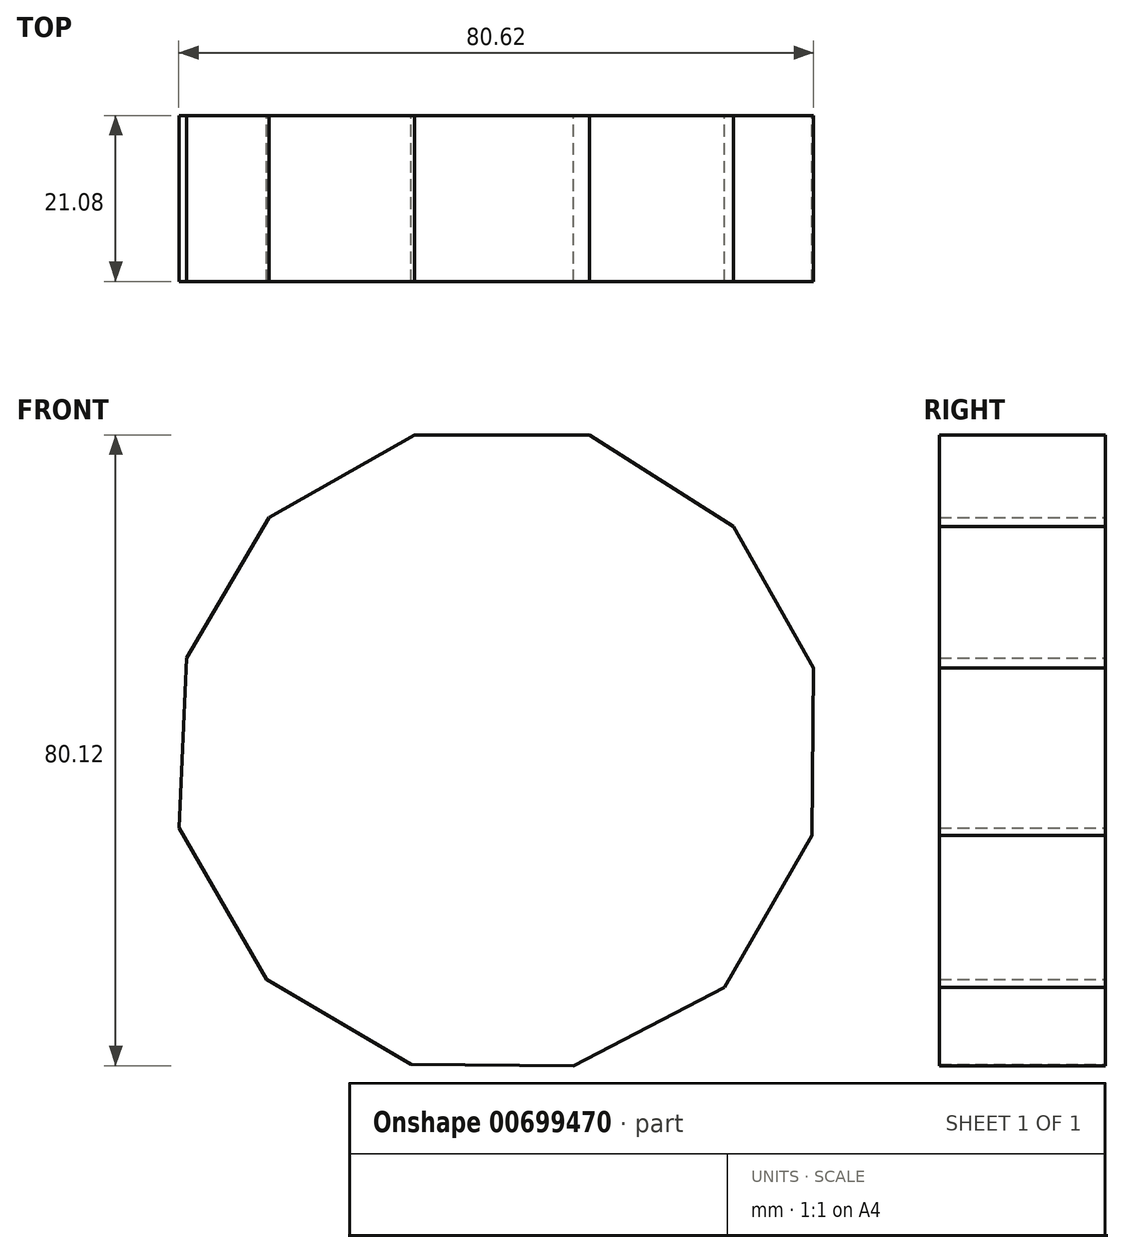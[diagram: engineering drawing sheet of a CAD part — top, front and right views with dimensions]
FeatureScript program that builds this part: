
annotation { "Feature Type Name" : "Feature", "Feature Type Description" : "" }
export const myFeature = defineFeature(function(context is Context, id is Id, definition is map)
    precondition{}
    {
        {
            var Q0;
            Q0=qCreatedBy(makeId("Front.planeOp"),FACE);
            var sketch = newSketch(context, id + "F0", { "sketchPlane" : qUnion([Q0])});
            skCircle(sketch, "E0.cCircle", {"center": v(0, 0) * mm, "radius": 76.52 * mm, "construction": true});
            skLineSegment(sketch, "E0.0", {"start": v(-76.41, 44.37) * mm, "end": v(0.21, 88.36) * mm});
            skLineSegment(sketch, "E0.1", {"start": v(0.21, 88.36) * mm, "end": v(76.63, 44) * mm});
            skLineSegment(sketch, "E0.2", {"start": v(76.63, 44) * mm, "end": v(76.41, -44.37) * mm});
            skLineSegment(sketch, "E0.3", {"start": v(76.41, -44.37) * mm, "end": v(-0.21, -88.36) * mm});
            skLineSegment(sketch, "E0.4", {"start": v(-0.21, -88.36) * mm, "end": v(-76.63, -44) * mm});
            skLineSegment(sketch, "E0.5", {"start": v(-76.63, -44) * mm, "end": v(-76.41, 44.37) * mm});
            skPoint(sketch, "E0.0.midPoint", {"position": v(-38.1, 66.36) * mm});
            skCircle(sketch, "E1.cCircle", {"center": v(0, 0) * mm, "radius": 40.02 * mm, "construction": true});
            skLineSegment(sketch, "E1.0", {"start": v(-80.05, 0.63) * mm, "end": v(40.57, 69) * mm});
            skLineSegment(sketch, "E1.1", {"start": v(40.57, 69) * mm, "end": v(39.48, -69.64) * mm});
            skLineSegment(sketch, "E1.2", {"start": v(39.48, -69.64) * mm, "end": v(-80.05, 0.63) * mm});
            skPoint(sketch, "E1.0.midPoint", {"position": v(-19.74, 34.82) * mm});
            skLineSegment(sketch, "E2.0", {"start": v(-36.9, 71.04) * mm, "end": v(79.97, -3.57) * mm});
            skLineSegment(sketch, "E2.1", {"start": v(79.97, -3.57) * mm, "end": v(-43.07, -67.47) * mm});
            skLineSegment(sketch, "E2.2", {"start": v(-43.07, -67.47) * mm, "end": v(-36.9, 71.04) * mm});
            skPoint(sketch, "E2.0.midPoint", {"position": v(21.54, 33.74) * mm});
            skLineSegment(sketch, "E3.0", {"start": v(-69.64, -39.48) * mm, "end": v(0.63, 80.05) * mm});
            skLineSegment(sketch, "E3.1", {"start": v(0.63, 80.05) * mm, "end": v(69, -40.57) * mm});
            skLineSegment(sketch, "E3.2", {"start": v(69, -40.57) * mm, "end": v(-69.64, -39.48) * mm});
            skPoint(sketch, "E3.0.midPoint", {"position": v(-34.5, 20.28) * mm});
            skLineSegment(sketch, "E4.0", {"start": v(-69.32, 40.02) * mm, "end": v(69.32, 40.02) * mm});
            skLineSegment(sketch, "E4.1", {"start": v(69.32, 40.02) * mm, "end": v(0, -80.05) * mm});
            skLineSegment(sketch, "E4.2", {"start": v(0, -80.05) * mm, "end": v(-69.32, 40.02) * mm});
            skPoint(sketch, "E4.0.midPoint", {"position": v(0, 40.02) * mm});
            skCircle(sketch, "E5.cCircle", {"center": v(0, 0) * mm, "radius": 17.05 * mm, "construction": true});
            skLineSegment(sketch, "E5.0", {"start": v(-34.1, 0.2) * mm, "end": v(17.21, 29.43) * mm});
            skLineSegment(sketch, "E5.1", {"start": v(17.21, 29.43) * mm, "end": v(16.88, -29.62) * mm});
            skLineSegment(sketch, "E5.2", {"start": v(16.88, -29.62) * mm, "end": v(-34.1, 0.2) * mm});
            skPoint(sketch, "E5.0.midPoint", {"position": v(-8.44, 14.8) * mm});
            skSolve(sketch);
        }
        {
            var Q0;
            Q0=makeQuery(id+"F0.imprint","IMPRINT",FACE,{"disambiguationData":[TD([[makeQuery(id+"F0.imprint","IMPRINT",EDGE,{"derivedFrom":sQuery(id+"F0.wireOp",EDGE,"E5.0")}),-1.0]])]});
            var Q1;
            Q1=makeQuery(id+"F0.imprint","IMPRINT",FACE,{"disambiguationData":[TD([[makeQuery(id+"F0.imprint","IMPRINT",EDGE,{"derivedFrom":sQuery(id+"F0.wireOp",EDGE,"E5.0")}),1.0]])]});
            extrude(context, id + "F1", {"entities" : qUnion([Q0, Q1]), "depth" : 21.08 * mm, "offsetDistance" : 25.4 * mm});
        }
    });
